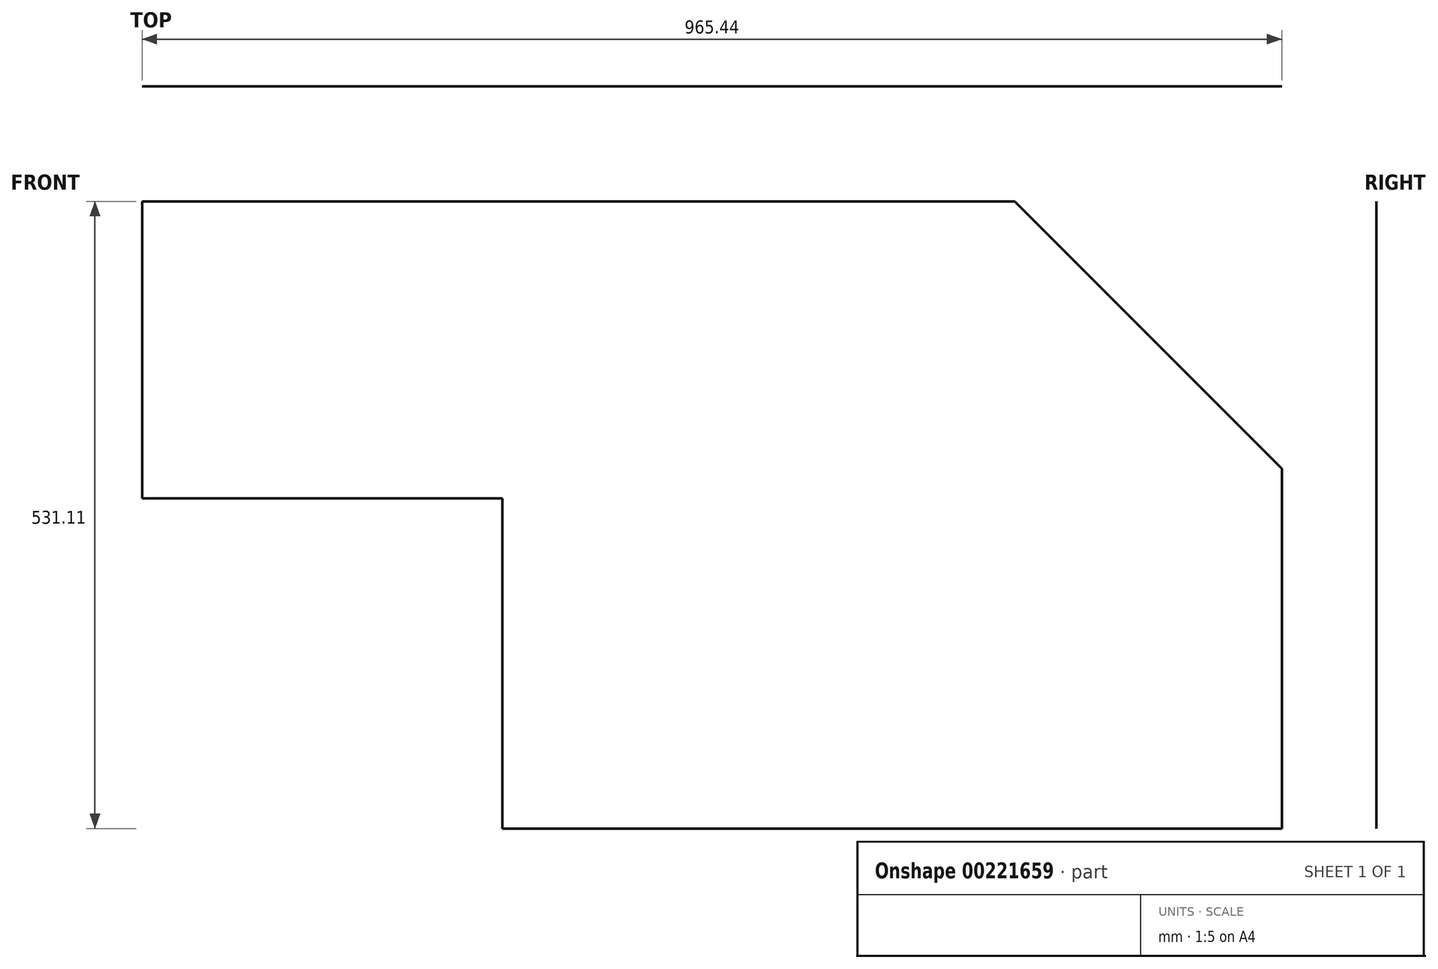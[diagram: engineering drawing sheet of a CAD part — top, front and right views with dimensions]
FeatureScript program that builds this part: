
annotation { "Feature Type Name" : "Feature", "Feature Type Description" : "" }
export const myFeature = defineFeature(function(context is Context, id is Id, definition is map)
    precondition{}
    {
        {
            var Q0;
            Q0=qCreatedBy(makeId("Front.planeOp"),FACE);
            var sketch = newSketch(context, id + "F0", { "sketchPlane" : qUnion([Q0])});
            skLineSegment(sketch, "E0", {"start": v(-447.43, 123.16) * mm, "end": v(-142.39, 123.16) * mm});
            skLineSegment(sketch, "E1", {"start": v(-142.39, 123.16) * mm, "end": v(-142.39, -156.49) * mm});
            skLineSegment(sketch, "E2", {"start": v(-142.39, -156.49) * mm, "end": v(518.01, -156.49) * mm});
            skLineSegment(sketch, "E3", {"start": v(518.01, -156.49) * mm, "end": v(518.01, 148.31) * mm});
            skLineSegment(sketch, "E4", {"start": v(518.01, 148.31) * mm, "end": v(291.7, 374.62) * mm});
            skLineSegment(sketch, "E5", {"start": v(291.7, 374.62) * mm, "end": v(-447.43, 374.62) * mm});
            skLineSegment(sketch, "E6", {"start": v(-447.43, 374.62) * mm, "end": v(-447.43, 123.16) * mm});
            skSolve(sketch);
        }
        {
            var Q0;
            Q0=makeQuery(id+"F0.imprint","IMPRINT",FACE,{"disambiguationData":[TD([[makeQuery(id+"F0.imprint","IMPRINT",EDGE,{"derivedFrom":sQuery(id+"F0.wireOp",EDGE,"E0")}),1.0]])]});
            extrude(context, id + "F1", {"entities" : qUnion([Q0]), "depth" : 1 / 2057.4 * mm});
        }
    });
